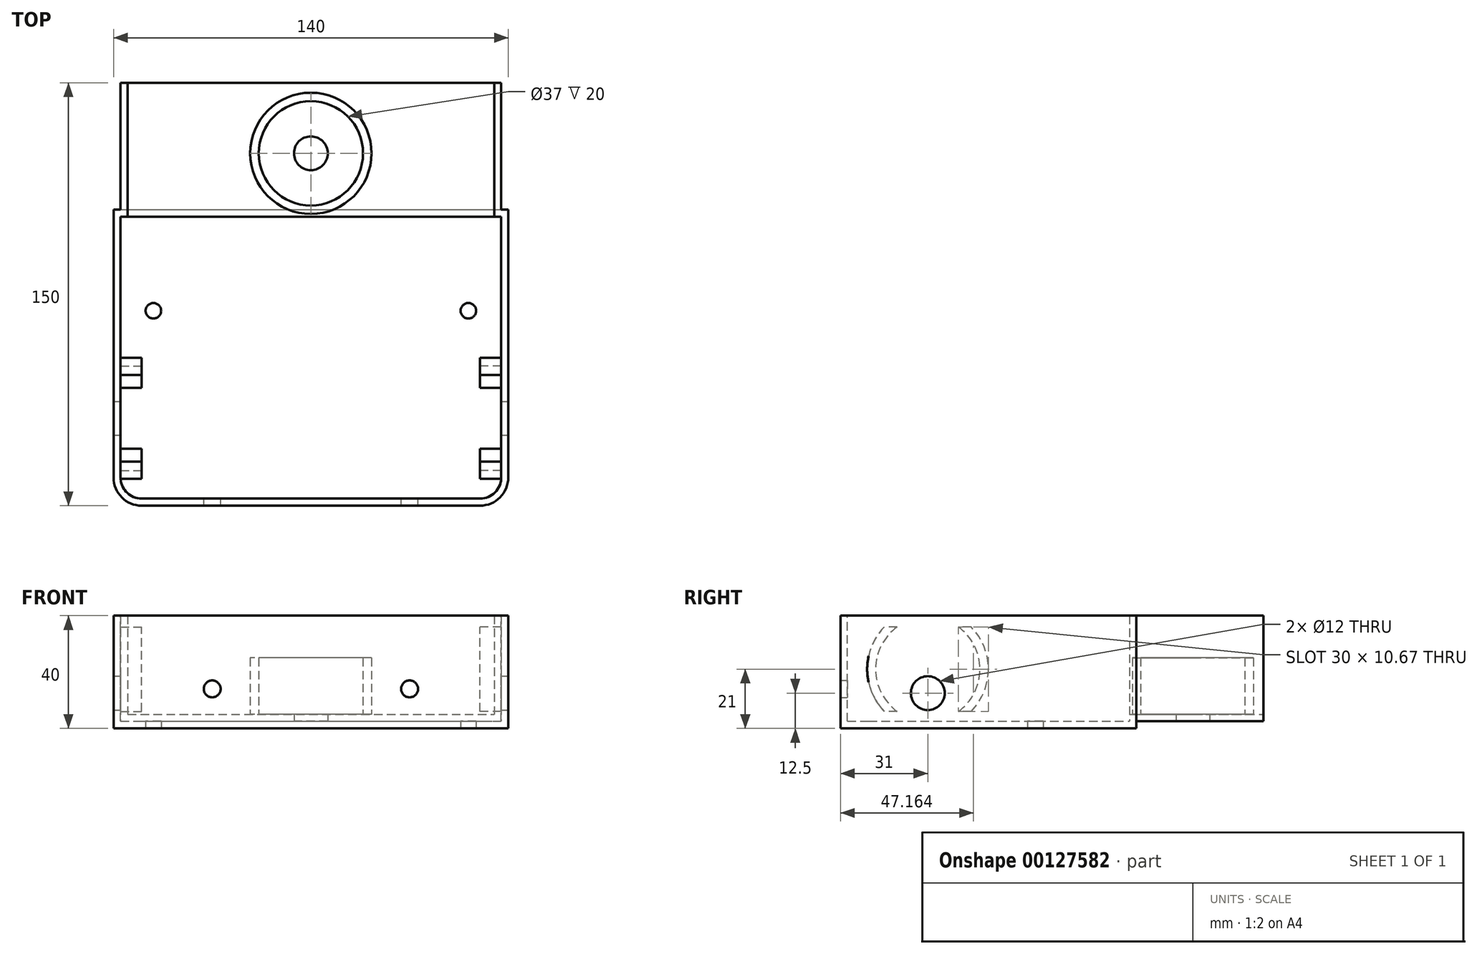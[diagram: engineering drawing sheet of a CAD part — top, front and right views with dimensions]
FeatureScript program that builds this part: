
annotation { "Feature Type Name" : "Feature", "Feature Type Description" : "" }
export const myFeature = defineFeature(function(context is Context, id is Id, definition is map)
    precondition{}
    {
        {
            var Q0;
            Q0=qCreatedBy(makeId("Top.planeOp"),FACE);
            var sketch = newSketch(context, id + "F0", { "sketchPlane" : qUnion([Q0])});
            skLineSegment(sketch, "E0.bottom", {"start": v(-70, -25) * mm, "end": v(70, -25) * mm});
            skLineSegment(sketch, "E0.top", {"start": v(-70, 125) * mm, "end": v(70, 125) * mm});
            skLineSegment(sketch, "E0.left", {"start": v(-70, -25) * mm, "end": v(-70, 125) * mm});
            skLineSegment(sketch, "E0.right", {"start": v(70, -25) * mm, "end": v(70, 125) * mm});
            skSolve(sketch);
        }
        {
            var Q0;
            Q0=makeQuery(id+"F0.imprint","IMPRINT",FACE,{"disambiguationData":[TD([[makeQuery(id+"F0.imprint","IMPRINT",EDGE,{"derivedFrom":sQuery(id+"F0.wireOp",EDGE,"E0.bottom")}),1.0]])]});
            extrude(context, id + "F1", {"entities" : qUnion([Q0]), "depth" : 40 * mm});
        }
        {
            var Q0;
            Q0=makeQuery(id+"F1.opExtrude","SWEPT_EDGE",EDGE,{"disambiguationData":[OSD([sQuery(id+"F0.wireOp",EDGE,"E0.bottom"),sQuery(id+"F0.wireOp",EDGE,"E0.left")])]});
            var Q1;
            Q1=makeQuery(id+"F1.opExtrude","SWEPT_EDGE",EDGE,{"disambiguationData":[OSD([sQuery(id+"F0.wireOp",EDGE,"E0.bottom"),sQuery(id+"F0.wireOp",EDGE,"E0.right")])]});
            fillet(context, id + "F2", {"entities" : qUnion([Q0, Q1]), "radius" : 10 * mm, "tangentPropagation" : true, "allowEdgeOverflow" : false});
        }
        {
            var Q0;
            Q0=qCreatedBy(makeId("Top.planeOp"),FACE);
            var sketch = newSketch(context, id + "F3", { "sketchPlane" : qUnion([Q0])});
            skLineSegment(sketch, "E1.bottom", {"start": v(-100, 180) * mm, "end": v(100, 180) * mm});
            skLineSegment(sketch, "E1.top", {"start": v(-100, 80) * mm, "end": v(100, 80) * mm});
            skLineSegment(sketch, "E1.left", {"start": v(-100, 180) * mm, "end": v(-100, 80) * mm});
            skLineSegment(sketch, "E1.right", {"start": v(100, 180) * mm, "end": v(100, 80) * mm});
            skSolve(sketch);
        }
        {
            var Q0;
            Q0=makeQuery(id+"F3.imprint","IMPRINT",FACE,{"disambiguationData":[TD([[makeQuery(id+"F3.imprint","IMPRINT",EDGE,{"derivedFrom":sQuery(id+"F3.wireOp",EDGE,"E1.bottom")}),-1.0]])]});
            extrude(context, id + "F4", {"entities" : qUnion([Q0]), "operationType" : NewBodyOperationType.REMOVE, "depth" : 2.5 * mm});
        }
        {
            var Q0;
            Q0=qCreatedBy(makeId("Top.planeOp"),FACE);
            var sketch = newSketch(context, id + "F5", { "sketchPlane" : qUnion([Q0])});
            skLineSegment(sketch, "E2.bottom", {"start": v(-107.5, 140) * mm, "end": v(-67.5, 140) * mm});
            skLineSegment(sketch, "E2.top", {"start": v(-107.5, 80) * mm, "end": v(-67.5, 80) * mm});
            skLineSegment(sketch, "E2.left", {"start": v(-107.5, 140) * mm, "end": v(-107.5, 80) * mm});
            skLineSegment(sketch, "E2.right", {"start": v(-67.5, 140) * mm, "end": v(-67.5, 80) * mm});
            skLineSegment(sketch, "E3.bottom", {"start": v(67.5, 140) * mm, "end": v(107.5, 140) * mm});
            skLineSegment(sketch, "E3.top", {"start": v(67.5, 80) * mm, "end": v(107.5, 80) * mm});
            skLineSegment(sketch, "E3.left", {"start": v(67.5, 140) * mm, "end": v(67.5, 80) * mm});
            skLineSegment(sketch, "E3.right", {"start": v(107.5, 140) * mm, "end": v(107.5, 80) * mm});
            skSolve(sketch);
        }
        {
            var Q0;
            Q0=qSketchRegion(id+"F5",true);
            extrude(context, id + "F6", {"entities" : qUnion([Q0]), "operationType" : NewBodyOperationType.REMOVE, "depth" : 200 * mm});
        }
        {
            var Q0;
            Q0=makeQuery(id+"F1.opExtrude","CAP_FACE",FACE,{"disambiguationData":[OSD([sQuery(id+"F0.wireOp",EDGE,"E0.bottom"),sQuery(id+"F0.wireOp",EDGE,"E0.top"),sQuery(id+"F0.wireOp",EDGE,"E0.left"),sQuery(id+"F0.wireOp",EDGE,"E0.right")])],"isStart":false});
            var Q1;
            Q1=makeQuery(id+"F1.opExtrude","SWEPT_FACE",FACE,{"disambiguationData":[OSD([sQuery(id+"F0.wireOp",EDGE,"E0.top")])]});
            shell(context, id + "F7", {"entities" : qUnion([Q0, Q1]), "thickness" : 2.5 * mm});
        }
        {
            var Q0;
            Q0=qCreatedBy(makeId("Top.planeOp"),FACE);
            var sketch = newSketch(context, id + "F8", { "sketchPlane" : qUnion([Q0])});
            skCircle(sketch, "E4", {"center": v(0, 100) * mm, "radius": 6 * mm});
            skSolve(sketch);
        }
        {
            var Q0;
            Q0=makeQuery(id+"F8.imprint","IMPRINT",FACE,{"disambiguationData":[TD([[makeQuery(id+"F8.imprint","IMPRINT",EDGE,{"derivedFrom":sQuery(id+"F8.wireOp",EDGE,"E4")}),1.0]])]});
            extrude(context, id + "F9", {"entities" : qUnion([Q0]), "operationType" : NewBodyOperationType.REMOVE, "depth" : 25 * mm});
        }
        {
            var Q0;
            Q0=qCreatedBy(makeId("Top.planeOp"),FACE);
            var sketch = newSketch(context, id + "F10", { "sketchPlane" : qUnion([Q0])});
            skCircle(sketch, "E5", {"center": v(0, 100) * mm, "radius": 21.5 * mm});
            skCircle(sketch, "E6", {"center": v(0, 100) * mm, "radius": 18.5 * mm});
            skSolve(sketch);
        }
        {
            var Q0;
            Q0=makeQuery(id+"F10.imprint","IMPRINT",FACE,{"disambiguationData":[TD([[makeQuery(id+"F10.imprint","IMPRINT",EDGE,{"derivedFrom":sQuery(id+"F10.wireOp",EDGE,"E5")}),1.0]])]});
            extrude(context, id + "F11", {"entities" : qUnion([Q0]), "operationType" : NewBodyOperationType.ADD, "depth" : 25 * mm, "hasSecondDirection" : true, "secondDirectionOppositeDirection" : false, "secondDirectionDepth" : 3 * mm});
        }
        {
            var Q0;
            Q0=qCreatedBy(makeId("Top.planeOp"),FACE);
            var sketch = newSketch(context, id + "F12", { "sketchPlane" : qUnion([Q0])});
            skCircle(sketch, "E7", {"center": v(-55.86, 44.14) * mm, "radius": 2.75 * mm});
            skCircle(sketch, "E8", {"center": v(55.86, 44.14) * mm, "radius": 2.75 * mm});
            skLineSegment(sketch, "E9", {"start": v(-55.86, 44.14) * mm, "end": v(0, 100) * mm, "construction": true});
            skLineSegment(sketch, "E10", {"start": v(0, 100) * mm, "end": v(55.86, 44.14) * mm, "construction": true});
            skSolve(sketch);
        }
        {
            var Q0;
            Q0=qSketchRegion(id+"F12",true);
            extrude(context, id + "F13", {"entities" : qUnion([Q0]), "operationType" : NewBodyOperationType.REMOVE, "depth" : 25 * mm});
        }
        {
            var Q0;
            Q0=qCreatedBy(makeId("Right.planeOp"),FACE);
            var sketch = newSketch(context, id + "F14", { "sketchPlane" : qUnion([Q0])});
            skCircle(sketch, "E11", {"center": v(6, 21) * mm, "radius": 18.5 * mm});
            skCircle(sketch, "E12", {"center": v(6, 21) * mm, "radius": 21.5 * mm});
            skLineSegment(sketch, "E13.bottom", {"start": v(-34, 36) * mm, "end": v(46, 36) * mm});
            skLineSegment(sketch, "E13.top", {"start": v(-34, 6) * mm, "end": v(46, 6) * mm});
            skLineSegment(sketch, "E13.left", {"start": v(-34, 36) * mm, "end": v(-34, 6) * mm});
            skLineSegment(sketch, "E13.right", {"start": v(46, 36) * mm, "end": v(46, 6) * mm});
            skSolve(sketch);
        }
        {
            var Q0;
            {var subQ0=sQuery(id+"F14.wireOp",EDGE,"E13.bottom");var subQ1=sQuery(id+"F14.wireOp",EDGE,"E11");var subQ2=makeQuery(id+"F14.imprint","INTERSECT",VERTEX,{"disambiguationData":[OD(0.0)],"derivedFrom":[subQ1,subQ0]});Q0=makeQuery(id+"F14.imprint","IMPRINT",FACE,{"disambiguationData":[TD([[makeQuery(id+"F14.imprint","IMPRINT",EDGE,{"disambiguationData":[TD([[subQ2,-1.0]])],"derivedFrom":subQ1}),-1.0]])]});}
            var Q1;
            {var subQ0=sQuery(id+"F14.wireOp",EDGE,"E13.bottom");var subQ1=sQuery(id+"F14.wireOp",EDGE,"E11");var subQ2=makeQuery(id+"F14.imprint","INTERSECT",VERTEX,{"disambiguationData":[OD(1.0)],"derivedFrom":[subQ1,subQ0]});Q1=makeQuery(id+"F14.imprint","IMPRINT",FACE,{"disambiguationData":[TD([[makeQuery(id+"F14.imprint","IMPRINT",EDGE,{"disambiguationData":[TD([[subQ2,1.0]])],"derivedFrom":subQ1}),-1.0]])]});}
            extrude(context, id + "F15", {"entities" : qUnion([Q0, Q1]), "operationType" : NewBodyOperationType.ADD, "depth" : 70 * mm, "hasSecondDirection" : true, "secondDirectionOppositeDirection" : false, "secondDirectionDepth" : 60 * mm});
        }
        {
            var Q0;
            {var subQ0=sQuery(id+"F14.wireOp",EDGE,"E13.bottom");var subQ1=sQuery(id+"F14.wireOp",EDGE,"E11");var subQ2=makeQuery(id+"F14.imprint","INTERSECT",VERTEX,{"disambiguationData":[OD(0.0)],"derivedFrom":[subQ1,subQ0]});Q0=makeQuery(id+"F14.imprint","IMPRINT",FACE,{"disambiguationData":[TD([[makeQuery(id+"F14.imprint","IMPRINT",EDGE,{"disambiguationData":[TD([[subQ2,-1.0]])],"derivedFrom":subQ1}),-1.0]])]});}
            var Q1;
            {var subQ0=sQuery(id+"F14.wireOp",EDGE,"E13.bottom");var subQ1=sQuery(id+"F14.wireOp",EDGE,"E11");var subQ2=makeQuery(id+"F14.imprint","INTERSECT",VERTEX,{"disambiguationData":[OD(1.0)],"derivedFrom":[subQ1,subQ0]});Q1=makeQuery(id+"F14.imprint","IMPRINT",FACE,{"disambiguationData":[TD([[makeQuery(id+"F14.imprint","IMPRINT",EDGE,{"disambiguationData":[TD([[subQ2,1.0]])],"derivedFrom":subQ1}),-1.0]])]});}
            extrude(context, id + "F16", {"entities" : qUnion([Q0, Q1]), "operationType" : NewBodyOperationType.ADD, "oppositeDirection" : true, "depth" : 70 * mm, "hasSecondDirection" : true, "secondDirectionOppositeDirection" : true, "secondDirectionDepth" : 60 * mm});
        }
        {
            var Q0;
            Q0=qCreatedBy(makeId("Right.planeOp"),FACE);
            var sketch = newSketch(context, id + "F17", { "sketchPlane" : qUnion([Q0])});
            skCircle(sketch, "E14", {"center": v(6, 12.5) * mm, "radius": 6 * mm});
            skSolve(sketch);
        }
        {
            var Q0;
            Q0=makeQuery(id+"F17.imprint","IMPRINT",FACE,{"disambiguationData":[TD([[makeQuery(id+"F17.imprint","IMPRINT",EDGE,{"derivedFrom":sQuery(id+"F17.wireOp",EDGE,"E14")}),1.0]])]});
            extrude(context, id + "F18", {"entities" : qUnion([Q0]), "operationType" : NewBodyOperationType.REMOVE, "oppositeDirection" : true, "depth" : 300 * mm, "hasSecondDirection" : true, "secondDirectionOppositeDirection" : false, "secondDirectionDepth" : 300 * mm});
        }
        {
            var Q0;
            Q0=qCreatedBy(makeId("Front.planeOp"),FACE);
            var sketch = newSketch(context, id + "F19", { "sketchPlane" : qUnion([Q0])});
            skCircle(sketch, "E15", {"center": v(-35, 14) * mm, "radius": 3 * mm});
            skCircle(sketch, "E16", {"center": v(35, 14) * mm, "radius": 3 * mm});
            skSolve(sketch);
        }
        {
            var Q0;
            Q0=makeQuery(id+"F19.imprint","IMPRINT",FACE,{"disambiguationData":[TD([[makeQuery(id+"F19.imprint","IMPRINT",EDGE,{"derivedFrom":sQuery(id+"F19.wireOp",EDGE,"E15")}),1.0]])]});
            var Q1;
            Q1=makeQuery(id+"F19.imprint","IMPRINT",FACE,{"disambiguationData":[TD([[makeQuery(id+"F19.imprint","IMPRINT",EDGE,{"derivedFrom":sQuery(id+"F19.wireOp",EDGE,"E16")}),1.0]])]});
            extrude(context, id + "F20", {"entities" : qUnion([Q0, Q1]), "operationType" : NewBodyOperationType.REMOVE, "depth" : 200 * mm});
        }
    });
